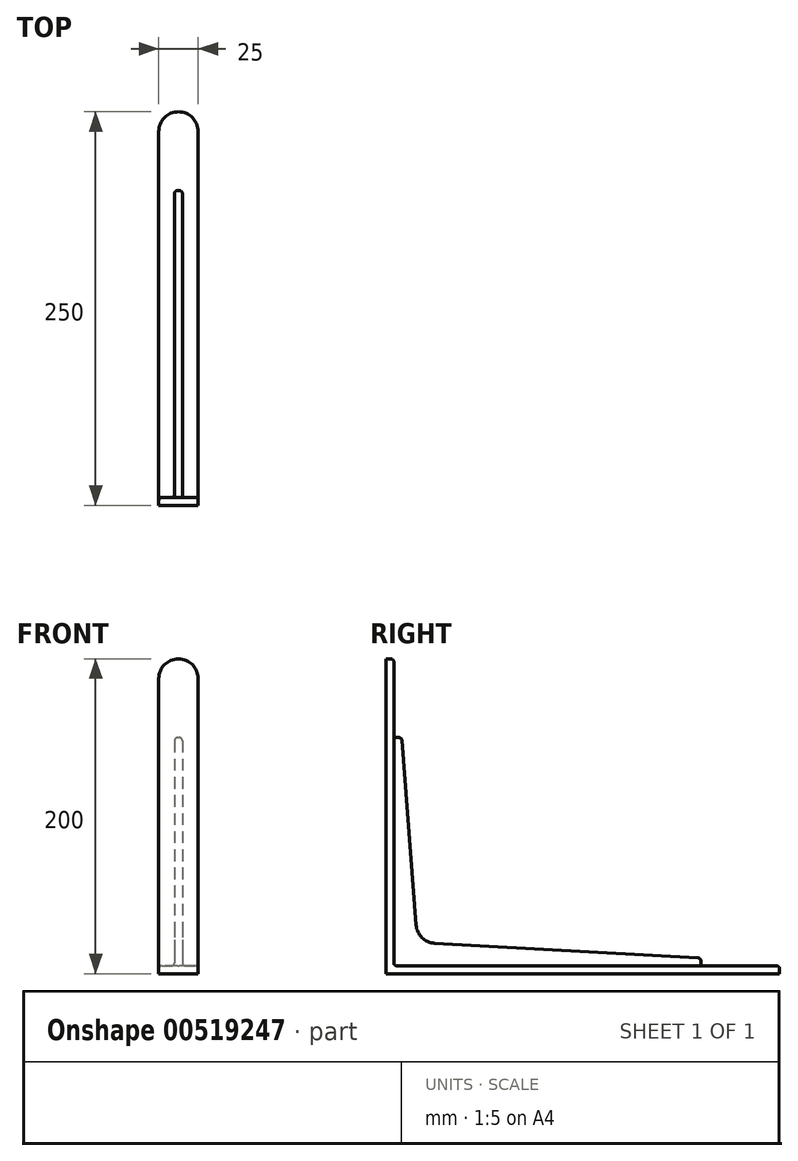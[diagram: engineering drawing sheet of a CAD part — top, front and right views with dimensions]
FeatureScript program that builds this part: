
annotation { "Feature Type Name" : "Feature", "Feature Type Description" : "" }
export const myFeature = defineFeature(function(context is Context, id is Id, definition is map)
    precondition{}
    {
        {
            var Q0;
            Q0=qCreatedBy(makeId("Right.planeOp"),FACE);
            var sketch = newSketch(context, id + "F0", { "sketchPlane" : qUnion([Q0])});
            skLineSegment(sketch, "E0.bottom", {"start": v(0, 0) * mm, "end": v(250, 0) * mm});
            skLineSegment(sketch, "E0.top", {"start": v(0, 200) * mm, "end": v(5, 200) * mm});
            skLineSegment(sketch, "E0.left", {"start": v(0, 0) * mm, "end": v(0, 200) * mm});
            skLineSegment(sketch, "E0.right", {"start": v(250, 0) * mm, "end": v(250, 5) * mm});
            skLineSegment(sketch, "E1.top", {"start": v(250, 5) * mm, "end": v(5, 5) * mm});
            skLineSegment(sketch, "E1.right", {"start": v(5, 200) * mm, "end": v(5, 5) * mm});
            skSolve(sketch);
        }
        {
            var Q0;
            Q0 = qSketchRegion(id + "F0", true);
            extrude(context, id + "F1", {"entities" : qUnion([Q0]), "oppositeDirection" : true, "depth" : 25 * mm, "offsetDistance" : 25 * mm});
        }
        {
            var Q0;
            Q0=qCreatedBy(makeId("Right.planeOp"),FACE);
            cPlane(context, id + "F2", {"entities" : qUnion([Q0]), "cplaneType" : CPlaneType.OFFSET, "offset" : 10 * mm, "oppositeDirection" : true, "width" : 150 * mm, "height" : 150 * mm});
        }
        {
            var Q0;
            Q0=qCreatedBy(id+"F2.planeOp",FACE);
            var sketch = newSketch(context, id + "F3", { "sketchPlane" : qUnion([Q0])});
            skLineSegment(sketch, "E2", {"start": v(0, 0) * mm, "end": v(95.79, 95.79) * mm, "construction": true});
            skLineSegment(sketch, "E3", {"start": v(0, 0) * mm, "end": v(0, 150) * mm, "construction": true});
            skLineSegment(sketch, "E4", {"start": v(0, 150) * mm, "end": v(5, 150) * mm, "construction": true});
            skLineSegment(sketch, "E5", {"start": v(5, 150) * mm, "end": v(10, 150) * mm});
            skLineSegment(sketch, "E6", {"start": v(10, 150) * mm, "end": v(20, 20) * mm});
            skLineSegment(sketch, "E7", {"start": v(20, 20) * mm, "end": v(200, 10) * mm});
            skLineSegment(sketch, "E8", {"start": v(200, 10) * mm, "end": v(200, 5) * mm});
            skLineSegment(sketch, "E9", {"start": v(200, 5) * mm, "end": v(200, 0) * mm, "construction": true});
            skLineSegment(sketch, "E10", {"start": v(200, 0) * mm, "end": v(0, 0) * mm, "construction": true});
            skLineSegment(sketch, "E11", {"start": v(5, 150) * mm, "end": v(5, 5) * mm});
            skLineSegment(sketch, "E12", {"start": v(5, 5) * mm, "end": v(200, 5) * mm});
            skSolve(sketch);
        }
        {
            var Q0;
            Q0 = qSketchRegion(id + "F3", true);
            extrude(context, id + "F4", {"entities" : qUnion([Q0]), "operationType" : NewBodyOperationType.ADD, "oppositeDirection" : true, "depth" : 5 * mm, "offsetDistance" : 25 * mm});
        }
        {
            var Q0;
            Q0=makeQuery(id+"F1.opExtrude","CAP_EDGE",EDGE,{"disambiguationData":[OSD([sQuery(id+"F0.wireOp",EDGE,"E0.top")])],"isStart":true});
            var Q1;
            Q1=makeQuery(id+"F1.opExtrude","CAP_EDGE",EDGE,{"disambiguationData":[OSD([sQuery(id+"F0.wireOp",EDGE,"E0.top")])],"isStart":false});
            var Q2;
            Q2=makeQuery(id+"F1.opExtrude","CAP_EDGE",EDGE,{"disambiguationData":[OSD([sQuery(id+"F0.wireOp",EDGE,"E0.right")])],"isStart":false});
            var Q3;
            Q3=makeQuery(id+"F1.opExtrude","CAP_EDGE",EDGE,{"disambiguationData":[OSD([sQuery(id+"F0.wireOp",EDGE,"E0.right")])],"isStart":true});
            var Q4;
            Q4=makeQuery(id+"F4.opExtrude","SWEPT_EDGE",EDGE,{"disambiguationData":[OSD([sQuery(id+"F3.wireOp",EDGE,"E6"),sQuery(id+"F3.wireOp",EDGE,"E7")])]});
            fillet(context, id + "F5", {"entities" : qUnion([Q0, Q1, Q2, Q3, Q4]), "radius" : 12.5 * mm, "tangentPropagation" : true, "allowEdgeOverflow" : false});
        }
        {
            var Q0;
            Q0=makeQuery(id+"F1.opExtrude","SWEPT_FACE",FACE,{"disambiguationData":[OSD([sQuery(id+"F0.wireOp",EDGE,"E1.right")])]});
            var Q1;
            Q1=makeQuery(id+"F4.opExtrude","SWEPT_FACE",FACE,{"disambiguationData":[OSD([sQuery(id+"F3.wireOp",EDGE,"E6")])]});
            var Q2;
            Q2=makeQuery(id+"F4.opExtrude","CAP_FACE",FACE,{"disambiguationData":[OSD([sQuery(id+"F3.wireOp",EDGE,"E5"),sQuery(id+"F3.wireOp",EDGE,"E6"),sQuery(id+"F3.wireOp",EDGE,"E7"),sQuery(id+"F3.wireOp",EDGE,"E8"),sQuery(id+"F3.wireOp",EDGE,"E11"),sQuery(id+"F3.wireOp",EDGE,"E12")])],"isStart":false});
            var Q3;
            Q3=makeQuery(id+"F4.opExtrude","CAP_FACE",FACE,{"disambiguationData":[OSD([sQuery(id+"F3.wireOp",EDGE,"E5"),sQuery(id+"F3.wireOp",EDGE,"E6"),sQuery(id+"F3.wireOp",EDGE,"E7"),sQuery(id+"F3.wireOp",EDGE,"E8"),sQuery(id+"F3.wireOp",EDGE,"E11"),sQuery(id+"F3.wireOp",EDGE,"E12")])],"isStart":true});
            var Q4;
            Q4=makeQuery(id+"F1.opExtrude","SWEPT_FACE",FACE,{"disambiguationData":[OSD([sQuery(id+"F0.wireOp",EDGE,"E1.top")])]});
            var Q5;
            Q5=makeQuery(id+"F4.opExtrude","SWEPT_FACE",FACE,{"disambiguationData":[OSD([sQuery(id+"F3.wireOp",EDGE,"E8")])]});
            fillet(context, id + "F6", {"entities" : qUnion([Q0, Q1, Q2, Q3, Q4, Q5]), "radius" : 2 * mm, "tangentPropagation" : true, "allowEdgeOverflow" : false});
        }
    });
